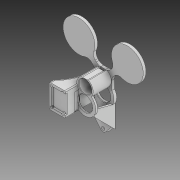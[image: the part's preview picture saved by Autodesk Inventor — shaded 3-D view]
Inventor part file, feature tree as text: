
AUTODESK INVENTOR PART (.ipt)
format: ipt  version: 2020 (Build 240168000, 168)  size: 516,608 bytes
history: native  units: mm
features: extrude x13, sketch x13, chamfer x4, fillet x2
ambient origin geometry x8: Origin, YZ Plane, XZ Plane, XY Plane, X Axis, Y Axis, Z Axis, Center Point
bodies: Solid1 (feature_tree)
feature tree (32):
  extrude  "Extrusion1"  Depth=23.8125mm
  extrude  "Extrusion2"  Depth=3.96875mm
  extrude  "Extrusion3"  Depth=9.797mm
  extrude  "Extrusion4"  Depth=16.1mm
  extrude  "Extrusion13"  Depth=14.15mm
  fillet  "Fillet4"  Radius=18.0mm
  chamfer  "Chamfer2"  Distance=20.0mm
  extrude  "Extrusion15"  Depth=2.0mm
  chamfer  "Chamfer3"  [1 undecoded]
  extrude  "Extrusion16"  Depth=1.0mm
  chamfer  "Chamfer4"  Distance=7.75mm
  extrude  "Extrusion17"  Depth=35.0mm
  extrude  "Extrusion18"  Depth=7.0mm
  extrude  "Extrusion19"  Depth=11.90625mm
  extrude  "Extrusion20"  TaperAngle=45.0deg  [1 undecoded]
  extrude  "Extrusion21"  Depth=26.876241mm
  extrude  "Extrusion22"  Depth=6.0mm
  fillet  "Fillet5"  Radius=3.5mm
  chamfer  "Chamfer5"  Distance=2.5mm
  sketch  "Sketch1"  dims[d0=20.6375mm d1=23.8125mm d2=32.816122mm]
  sketch  "Sketch2"  dims[d3=23.8125mm d4=3.96875mm]
  sketch  "Sketch3"  dims[d5=19.05mm d6=9.797mm]
  sketch  "Sketch4"  dims[d7=5.5mm d8=16.1mm]
  sketch  "Sketch13"  dims[d9=3.0mm d10=0.0mm d11=14.15mm d12=18.0mm d13=8.0mm]
  sketch  "Sketch15"  dims[d14=9.0mm d15=20.0mm d16=0.0mm]
  sketch  "Sketch16"  dims[d17=45.0deg d18=2.0mm d19=0.0mm d20=0.0mm]
  sketch  "Sketch17"  dims[d21=1.0mm d22=1.0mm]
  sketch  "Sketch18"  dims[d23=2.5mm d24=7.75mm d25=0.0mm]
  sketch  "Sketch19"  dims[d58=27.0mm d59=35.0mm]
  sketch  "Sketch20"  dims[d60=1.5mm d61=0.0mm d62=7.0mm]
  sketch  "Sketch21"  dims[d63=0.5mm d64=2.0mm d65=45.0deg d69=11.90625mm]
  sketch  "Sketch22"  dims[d70=45.0deg d71=45.0deg d72=26.876241mm d73=6.0mm d74=3.5mm d75=2.5mm d76=2.0mm d77=0.0mm d78=1.0mm d79=3.0mm d80=45.0deg d81=26.0mm d82=18.0mm d83=35.0mm d84=0.0mm d85=2.0mm d86=2.0mm d87=45.0deg d88=2.4mm d89=20.5mm d90=12.5mm d91=2.5mm d92=20.0mm d93=0.0mm d94=2.0mm d95=0.0mm d96=2.0mm d97=0.0mm d98=2.0mm d99=0.0mm d100=3.0mm d101=5.0mm d102=2.0mm d103=0.0mm d104=28.0mm d105=0.0mm d106=2.0mm d107=0.5mm d108=2.0mm d109=45.0deg d110=1.0mm]
note: 2 required parameter values undecoded (feature->parameter linkage not recoverable at this tier; creation-order binding heuristic only, values carry confidence <= 0.55)
